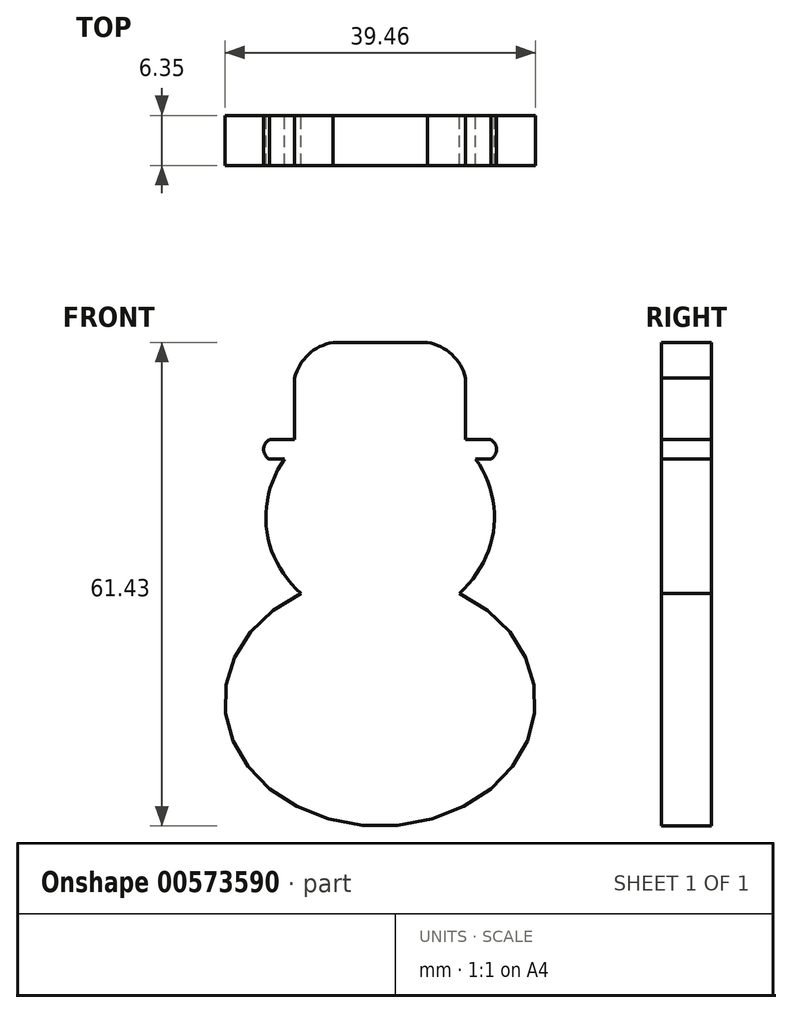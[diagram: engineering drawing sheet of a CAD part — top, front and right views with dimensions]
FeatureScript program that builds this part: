
annotation { "Feature Type Name" : "Feature", "Feature Type Description" : "" }
export const myFeature = defineFeature(function(context is Context, id is Id, definition is map)
    precondition{}
    {
        {
            var Q0;
            Q0=qCreatedBy(makeId("Front.planeOp"),FACE);
            var sketch = newSketch(context, id + "F0", { "sketchPlane" : qUnion([Q0])});
            skLineSegment(sketch, "E0", {"start": v(0, 62.5) * mm, "end": v(0, 0) * mm, "construction": true});
            skEllipticalArc(sketch, "E1", {});
            skEllipticalArc(sketch, "E2", {});
            skLineSegment(sketch, "E3", {"start": v(-12.14, 47.13) * mm, "end": v(-14.06, 47.13) * mm});
            skArc(sketch, "E4", {"start": v(-14.06, 49.63) * mm, "mid": v(-14.8, 48.38) * mm, "end": v(-14.06, 47.13) * mm});
            skLineSegment(sketch, "E5", {"start": v(-14.06, 49.63) * mm, "end": v(-10.85, 49.63) * mm});
            skLineSegment(sketch, "E6", {"start": v(-10.85, 49.63) * mm, "end": v(-10.85, 57.47) * mm});
            skArc(sketch, "E7", {"start": v(-6, 61.95) * mm, "mid": v(-9.1, 60.44) * mm, "end": v(-10.85, 57.47) * mm});
            skLineSegment(sketch, "E8", {"start": v(-6, 61.95) * mm, "end": v(0, 61.95) * mm});
            skEllipticalArc(sketch, "E9.MirrorCS", {});
            skEllipticalArc(sketch, "E10.MirrorCS", {});
            skLineSegment(sketch, "E11.MirrorCS", {"start": v(12.14, 47.13) * mm, "end": v(14.06, 47.13) * mm});
            skArc(sketch, "E12.MirrorCS", {"start": v(14.06, 49.63) * mm, "mid": v(14.8, 48.38) * mm, "end": v(14.06, 47.13) * mm});
            skLineSegment(sketch, "E13.MirrorCS", {"start": v(14.06, 49.63) * mm, "end": v(10.85, 49.63) * mm});
            skLineSegment(sketch, "E14.MirrorCS", {"start": v(10.85, 49.63) * mm, "end": v(10.85, 57.47) * mm});
            skArc(sketch, "E15.MirrorCS", {"start": v(6, 61.95) * mm, "mid": v(9.1, 60.44) * mm, "end": v(10.85, 57.47) * mm});
            skLineSegment(sketch, "E16.MirrorCS", {"start": v(6, 61.95) * mm, "end": v(0, 61.95) * mm});
            const initialGuessF0  = {"E1": [0, 0.01641230843961239, 1, 0, 0.019726332277059555, 0.015895011464542724, 2.105840860442348, 4.71238898038469], "E2": [0, 0.039768286049366, 1, 0, 0.014518579468131067, 0.013426131915251719, 2.5609857339731503, 3.9470646787178647], "E9.MirrorCS": [0, 0.01641230843961239, -1, 0, 0.019726332277059555, 0.015895011464542724, 1.5707963267948966, 4.177344446737238], "E10.MirrorCS": [0, 0.039768286049366, -1, 0, 0.014518579468131067, 0.013426131915251719, 2.3361206284617215, 3.722199573206436]};
            skSetInitialGuess(sketch, initialGuessF0);
            skSolve(sketch);
        }
        {
            var Q0;
            Q0 = qSketchRegion(id + "F0", true);
            extrude(context, id + "F1", {"entities" : qUnion([Q0]), "depth" : 6.35 * mm, "offsetDistance" : 25.4 * mm});
        }
    });
